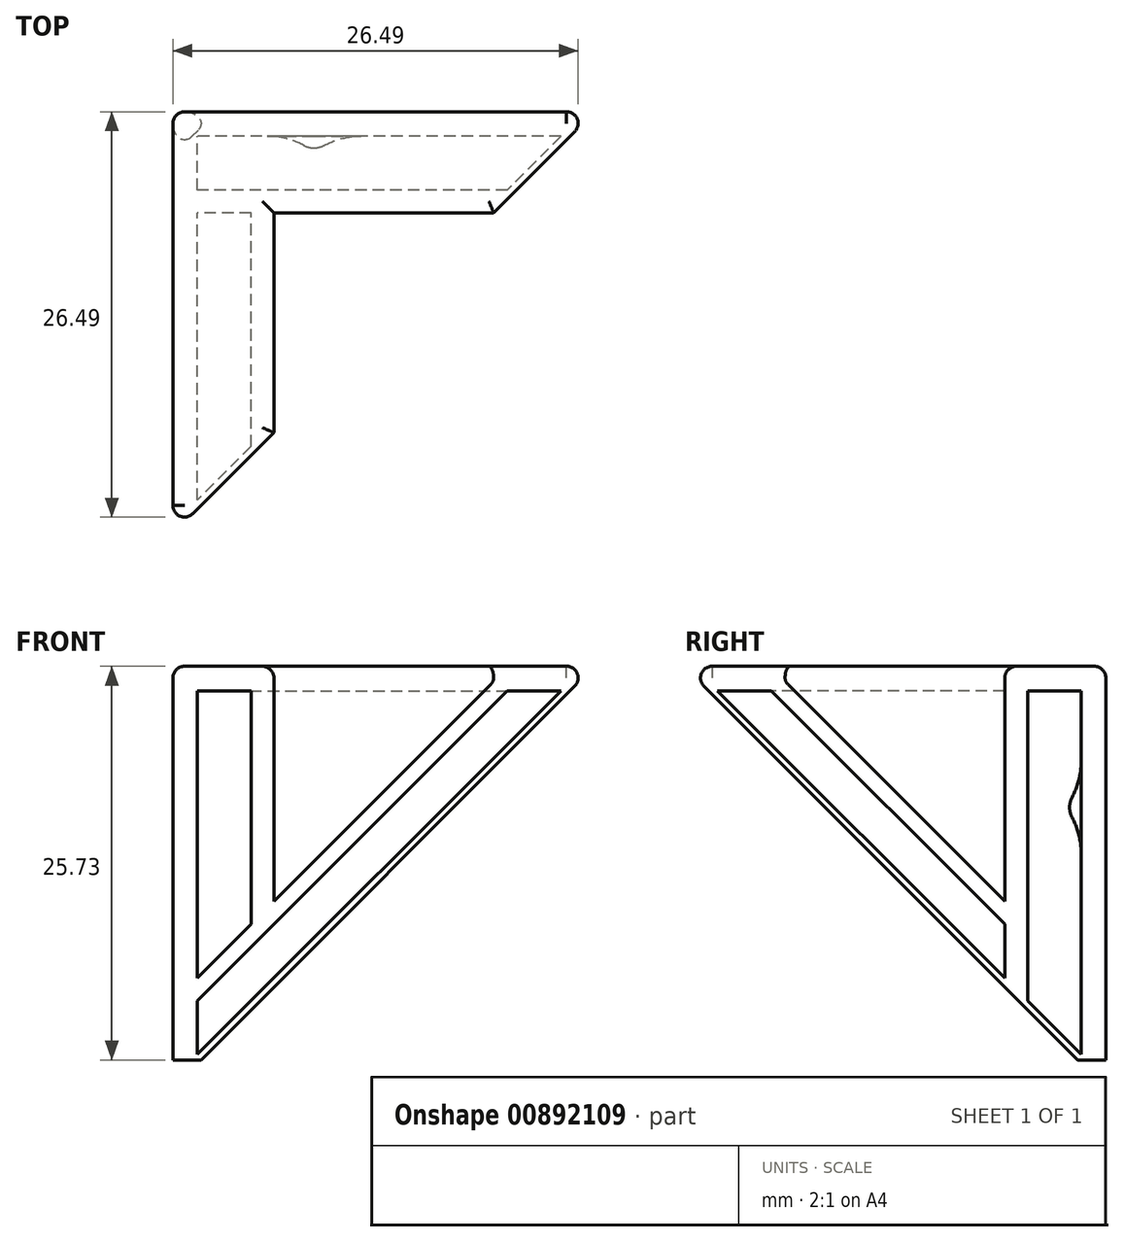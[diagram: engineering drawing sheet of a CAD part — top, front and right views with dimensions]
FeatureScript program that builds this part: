
annotation { "Feature Type Name" : "Feature", "Feature Type Description" : "" }
export const myFeature = defineFeature(function(context is Context, id is Id, definition is map)
    precondition{}
    {
        {
            var Q0;
            Q0=qCreatedBy(makeId("Top.planeOp"),FACE);
            var sketch = newSketch(context, id + "F0", { "sketchPlane" : qUnion([Q0])});
            skLineSegment(sketch, "E0", {"start": v(0, 0) * mm, "end": v(21.97, 0) * mm});
            skLineSegment(sketch, "E1", {"start": v(21.97, 0) * mm, "end": v(21.97, 6.6) * mm});
            skLineSegment(sketch, "E2", {"start": v(21.97, 6.6) * mm, "end": v(-6.6, 6.6) * mm});
            skLineSegment(sketch, "E3", {"start": v(-6.6, 6.6) * mm, "end": v(-6.6, -21.97) * mm});
            skLineSegment(sketch, "E4", {"start": v(-6.6, -21.97) * mm, "end": v(0, -21.97) * mm});
            skLineSegment(sketch, "E5", {"start": v(0, -21.97) * mm, "end": v(0, 0) * mm});
            skSolve(sketch);
        }
        {
            var Q0;
            Q0 = qSketchRegion(id + "F0", true);
            extrude(context, id + "F1", {"entities" : qUnion([Q0]), "oppositeDirection" : true, "depth" : 28.57 * mm, "offsetDistance" : 25.4 * mm});
        }
        {
            var Q0;
            Q0=makeQuery(id+"F1.opExtrude","CAP_VERTEX",VERTEX,{"disambiguationData":[OSD([sQuery(id+"F0.wireOp",EDGE,"E2"),sQuery(id+"F0.wireOp",EDGE,"E3")])],"isStart":false});
            var Q1;
            Q1=sQuery(id+"F0.wireOp",VERTEX,"E3.end");
            var Q2;
            Q2=sQuery(id+"F0.wireOp",VERTEX,"E1.end");
            cPlane(context, id + "F2", {"entities" : qUnion([Q0, Q1, Q2]), "cplaneType" : CPlaneType.THREE_POINT, "offset" : 25.4 * mm, "width" : 152.4 * mm, "height" : 152.4 * mm});
        }
        {
            var Q0;
            Q0=qCreatedBy(id+"F2.planeOp",FACE);
            var sketch = newSketch(context, id + "F3", { "sketchPlane" : qUnion([Q0])});
            skCircle(sketch, "E6", {"center": v(0, 0) * mm, "radius": 38.1 * mm});
            skSolve(sketch);
        }
        {
            var Q0;
            Q0 = qSketchRegion(id + "F3", true);
            extrude(context, id + "F4", {"entities" : qUnion([Q0]), "operationType" : NewBodyOperationType.REMOVE, "endBound" : BoundingType.THROUGH_ALL, "depth" : 25.4 * mm, "offsetDistance" : 25.4 * mm});
        }
        {
            var Q0;
            Q0=makeQuery(id+"F1.opExtrude","CAP_FACE",FACE,{"disambiguationData":[OSD([sQuery(id+"F0.wireOp",EDGE,"E0"),sQuery(id+"F0.wireOp",EDGE,"E1"),sQuery(id+"F0.wireOp",EDGE,"E2"),sQuery(id+"F0.wireOp",EDGE,"E3"),sQuery(id+"F0.wireOp",EDGE,"E4"),sQuery(id+"F0.wireOp",EDGE,"E5")])],"isStart":true});
            cPlane(context, id + "F5", {"entities" : qUnion([Q0]), "cplaneType" : CPlaneType.OFFSET, "offset" : 1.6 * mm, "oppositeDirection" : true, "width" : 152.4 * mm, "height" : 152.4 * mm});
        }
        {
            var Q0;
            Q0=qCreatedBy(id+"F5.planeOp",FACE);
            var sketch = newSketch(context, id + "F6", { "sketchPlane" : qUnion([Q0])});
            skLineSegment(sketch, "E7.bottom", {"start": v(-5, 5) * mm, "end": v(21.97, 5) * mm});
            skLineSegment(sketch, "E7.top", {"start": v(-5, 1.49) * mm, "end": v(21.97, 1.49) * mm});
            skLineSegment(sketch, "E7.left", {"start": v(-5, 5) * mm, "end": v(-5, 1.49) * mm});
            skLineSegment(sketch, "E7.right", {"start": v(21.97, 5) * mm, "end": v(21.97, 1.49) * mm});
            skLineSegment(sketch, "E8.bottom", {"start": v(-5, 0) * mm, "end": v(-1.49, 0) * mm});
            skLineSegment(sketch, "E8.top", {"start": v(-5, -21.97) * mm, "end": v(-1.49, -21.97) * mm});
            skLineSegment(sketch, "E8.left", {"start": v(-5, 0) * mm, "end": v(-5, -21.97) * mm});
            skLineSegment(sketch, "E8.right", {"start": v(-1.49, 0) * mm, "end": v(-1.49, -21.97) * mm});
            skSolve(sketch);
        }
        {
            var Q0;
            Q0 = qSketchRegion(id + "F6", true);
            extrude(context, id + "F7", {"entities" : qUnion([Q0]), "operationType" : NewBodyOperationType.REMOVE, "endBound" : BoundingType.THROUGH_ALL, "oppositeDirection" : true, "depth" : 25.4 * mm, "offsetDistance" : 25.4 * mm});
        }
        {
            var Q0;
            Q0=makeQuery(id+"F1.opExtrude","CAP_FACE",FACE,{"disambiguationData":[OSD([sQuery(id+"F0.wireOp",EDGE,"E0"),sQuery(id+"F0.wireOp",EDGE,"E1"),sQuery(id+"F0.wireOp",EDGE,"E2"),sQuery(id+"F0.wireOp",EDGE,"E3"),sQuery(id+"F0.wireOp",EDGE,"E4"),sQuery(id+"F0.wireOp",EDGE,"E5")])],"isStart":true});
            var Q1;
            Q1=makeQuery(id+"F1.opExtrude","SWEPT_FACE",FACE,{"disambiguationData":[OSD([sQuery(id+"F0.wireOp",EDGE,"E2")])]});
            var Q2;
            Q2=makeQuery(id+"F1.opExtrude","SWEPT_FACE",FACE,{"disambiguationData":[OSD([sQuery(id+"F0.wireOp",EDGE,"E3")])]});
            fillet(context, id + "F8", {"entities" : qUnion([Q0, Q1, Q2]), "radius" : 0.76 * mm, "tangentPropagation" : true, "allowEdgeOverflow" : false});
        }
        {
            var Q0;
            Q0=makeQuery(id+"F7.boolean.opBoolean","COPY",FACE,{"derivedFrom":makeQuery(id+"F7.opExtrude","SWEPT_FACE",FACE,{"disambiguationData":[OSD([sQuery(id+"F6.wireOp",EDGE,"E7.left")])]})});
            cPlane(context, id + "F9", {"entities" : qUnion([Q0]), "cplaneType" : CPlaneType.OFFSET, "offset" : 7.62 * mm, "width" : 152.4 * mm, "height" : 152.4 * mm});
        }
        {
            var Q0;
            Q0=qCreatedBy(id+"F9.planeOp",FACE);
            var sketch = newSketch(context, id + "F10", { "sketchPlane" : qUnion([Q0])});
            skLineSegment(sketch, "E9.0.1", {"start": v(5, -1.6) * mm, "end": v(5, -25.37) * mm, "construction": true});
            skLineSegment(sketch, "E9.0.2", {"start": v(5, -25.37) * mm, "end": v(5, -1.6) * mm, "construction": true});
            skLineSegment(sketch, "E10", {"start": v(5, -10.5) * mm, "end": v(5, -9.22) * mm});
            skLineSegment(sketch, "E11", {"start": v(5, -9.22) * mm, "end": v(4.24, -9.22) * mm});
            skLineSegment(sketch, "E12", {"start": v(4.24, -9.22) * mm, "end": v(4.24, -3.48) * mm, "construction": true});
            skArc(sketch, "E13", {"start": v(4.24, -9.22) * mm, "mid": v(4.45, -9.96) * mm, "end": v(5, -10.5) * mm});
            skSolve(sketch);
        }
        {
            var Q0;
            Q0 = qSketchRegion(id + "F10", true);
            var Q1;
            Q1=sQuery(id+"F10.wireOp",EDGE,"E11");
            revolve(context, id + "F11", {"operationType" : NewBodyOperationType.ADD, "surfaceOperationType" : NewSurfaceOperationType.NEW, "entities" : qUnion([Q0]), "axis" : qUnion([Q1]), "revolveType" : RevolveType.FULL});
        }
        {
            var Q0;
            Q0=makeQuery(id+"F1.opExtrude","CAP_FACE",FACE,{"disambiguationData":[OSD([sQuery(id+"F0.wireOp",EDGE,"E0"),sQuery(id+"F0.wireOp",EDGE,"E1"),sQuery(id+"F0.wireOp",EDGE,"E2"),sQuery(id+"F0.wireOp",EDGE,"E3"),sQuery(id+"F0.wireOp",EDGE,"E4"),sQuery(id+"F0.wireOp",EDGE,"E5")])],"isStart":true});
            var sketch = newSketch(context, id + "F12", { "sketchPlane" : qUnion([Q0])});
            skLineSegment(sketch, "E14", {"start": v(0, 0) * mm, "end": v(-5.84, 5.84) * mm, "construction": true});
            skSolve(sketch);
        }
        {
            var Q0;
            Q0=sQuery(id+"F12.wireOp",EDGE,"E14");
            var Q1;
            {var subQ0=sQuery(id+"F0.wireOp",EDGE,"E5");var subQ1=sQuery(id+"F0.wireOp",EDGE,"E3");var subQ2=sQuery(id+"F0.wireOp",EDGE,"E2");var subQ3=sQuery(id+"F0.wireOp",EDGE,"E0");var subQ4=makeQuery(id+"F1.opExtrude","CAP_FACE",FACE,{"disambiguationData":[OSD([subQ3,sQuery(id+"F0.wireOp",EDGE,"E1"),subQ2,subQ1,sQuery(id+"F0.wireOp",EDGE,"E4"),subQ0])],"isStart":true});var subQ5=subQ4;Q1=makeQuery(id+"F12.imprint","IMPRINT",FACE,{"disambiguationData":[TD([[makeQuery(id+"F12.imprint","IMPRINT",EDGE,{"derivedFrom":makeQuery(id+"F8.opFillet","BLEND_EDGE",EDGE,{"blendedFrom":[makeQuery(id+"F1.opExtrude","CAP_EDGE",EDGE,{"disambiguationData":[OSD([subQ2])],"isStart":true}),subQ5],"blendedInto":[subQ5]})}),1.0]])]});}
            cPlane(context, id + "F13", {"entities" : qUnion([Q0, Q1]), "cplaneType" : CPlaneType.LINE_ANGLE, "offset" : 25.4 * mm, "angle" : 90 * degree, "width" : 152.4 * mm, "height" : 152.4 * mm});
        }
        {
            var Q0;
            Q0=makeQuery(id+"F11.opRevolve","SWEPT_FACE",FACE,{"disambiguationData":[OSD([sQuery(id+"F10.wireOp",EDGE,"E13")])]});
            var Q1;
            Q1=makeQuery(id+"F63sKs5hCbV0KK5_1.1.F11.opRevolve","SWEPT_FACE",FACE,{"disambiguationData":[OSD([sQuery(id+"F10.wireOp",EDGE,"E13")])]});
            fillet(context, id + "F14", {"entities" : qUnion([Q0, Q1]), "radius" : 5.08 * mm, "tangentPropagation" : true, "allowEdgeOverflow" : false});
        }
        {
            var Q0;
            Q0=makeQuery(id+"F1.opExtrude","SWEPT_FACE",FACE,{"disambiguationData":[OSD([sQuery(id+"F0.wireOp",EDGE,"E3")])]});
            var sketch = newSketch(context, id + "F15", { "sketchPlane" : qUnion([Q0])});
            skLineSegment(sketch, "E15", {"start": v(19.67, -1.3) * mm, "end": v(-5.3, -26.27) * mm, "construction": true});
            skLineSegment(sketch, "E16.0", {"start": v(-6.6, -25.73) * mm, "end": v(-6.6, -0.76) * mm, "construction": true});
            skLineSegment(sketch, "E17.bottom", {"start": v(-6.6, -25.73) * mm, "end": v(-4.76, -25.73) * mm});
            skLineSegment(sketch, "E17.top", {"start": v(-6.6, -27.57) * mm, "end": v(-4.76, -27.57) * mm});
            skLineSegment(sketch, "E17.left", {"start": v(-6.6, -25.73) * mm, "end": v(-6.6, -27.57) * mm});
            skLineSegment(sketch, "E17.right", {"start": v(-4.76, -25.73) * mm, "end": v(-4.76, -27.57) * mm});
            skSolve(sketch);
        }
        {
            var Q0;
            Q0 = qSketchRegion(id + "F15", true);
            extrude(context, id + "F16", {"entities" : qUnion([Q0]), "operationType" : NewBodyOperationType.REMOVE, "endBound" : BoundingType.THROUGH_ALL, "oppositeDirection" : true, "depth" : 25.4 * mm, "offsetDistance" : 25.4 * mm});
        }
    });
